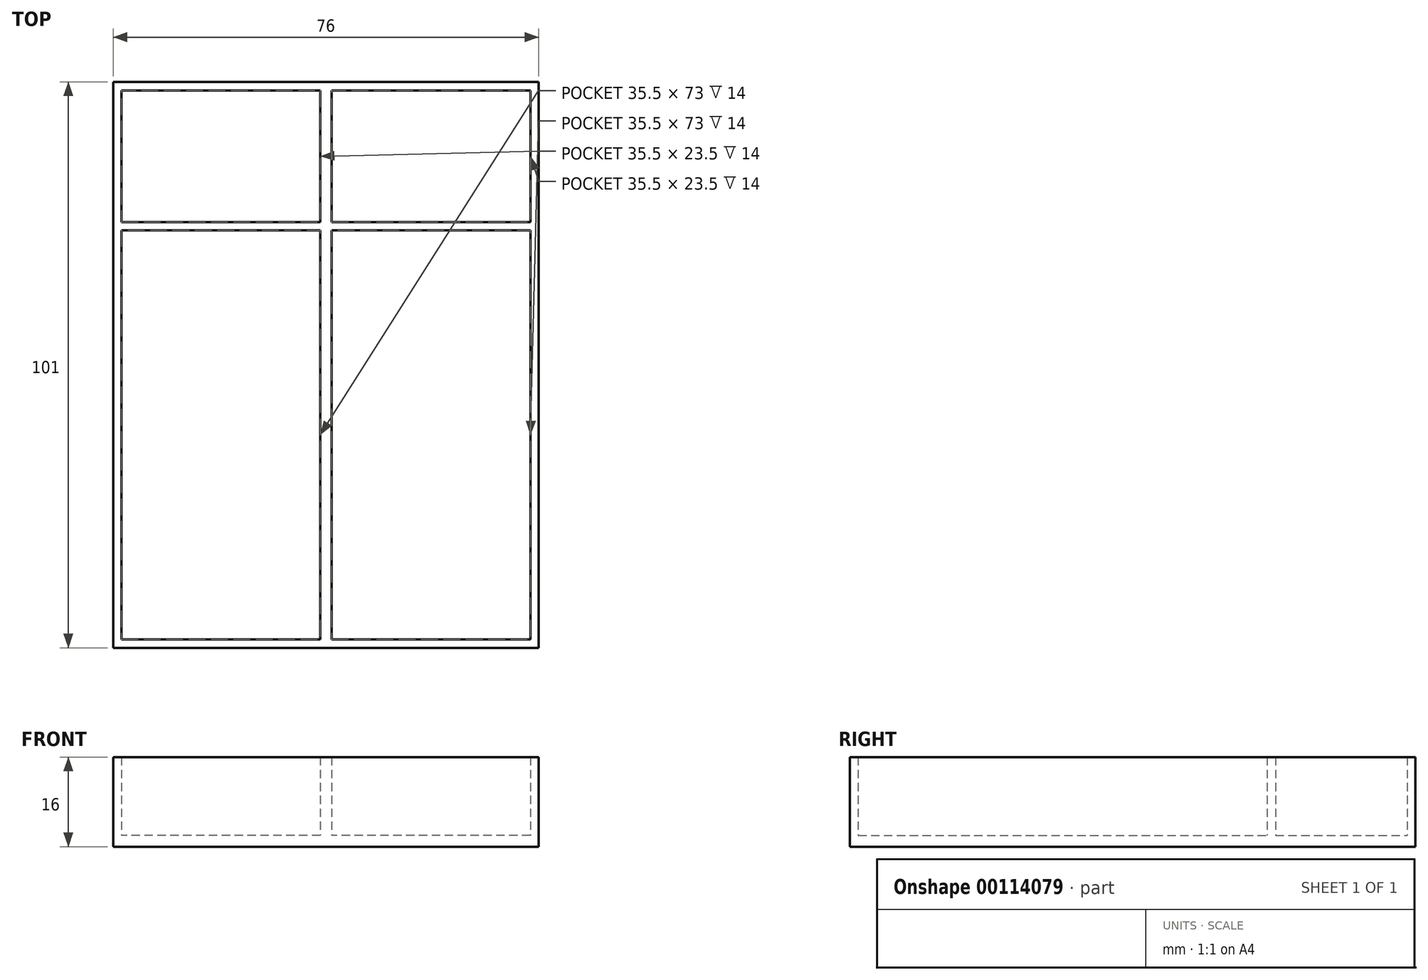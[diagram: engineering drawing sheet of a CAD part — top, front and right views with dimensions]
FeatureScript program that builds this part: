
annotation { "Feature Type Name" : "Feature", "Feature Type Description" : "" }
export const myFeature = defineFeature(function(context is Context, id is Id, definition is map)
    precondition{}
    {
        {
            var Q0;
            Q0=qCreatedBy(makeId("Top.planeOp"),FACE);
            var sketch = newSketch(context, id + "F0", { "sketchPlane" : qUnion([Q0])});
            skLineSegment(sketch, "E0.bottom", {"start": v(38, -38) * mm, "end": v(-38, -38) * mm});
            skLineSegment(sketch, "E0.top", {"start": v(38, 38) * mm, "end": v(-38, 38) * mm});
            skLineSegment(sketch, "E0.left", {"start": v(38, -38) * mm, "end": v(38, 38) * mm});
            skLineSegment(sketch, "E0.right", {"start": v(-38, -38) * mm, "end": v(-38, 38) * mm});
            skPoint(sketch, "E0.middle", {"position": v(0, 0) * mm});
            skLineSegment(sketch, "E1.bottom", {"start": v(-38, 38) * mm, "end": v(38, 38) * mm});
            skLineSegment(sketch, "E1.top", {"start": v(-38, 63) * mm, "end": v(38, 63) * mm});
            skLineSegment(sketch, "E1.left", {"start": v(-38, 38) * mm, "end": v(-38, 63) * mm});
            skLineSegment(sketch, "E1.right", {"start": v(38, 38) * mm, "end": v(38, 63) * mm});
            skLineSegment(sketch, "E2", {"start": v(-36.5, 38) * mm, "end": v(-36.5, 61.5) * mm});
            skLineSegment(sketch, "E3", {"start": v(-36.5, 61.5) * mm, "end": v(-1, 61.5) * mm});
            skLineSegment(sketch, "E4", {"start": v(36.5, 61.5) * mm, "end": v(36.5, 38) * mm});
            skLineSegment(sketch, "E5", {"start": v(-1, 38) * mm, "end": v(-1, 61.5) * mm});
            skLineSegment(sketch, "E6", {"start": v(1, 38) * mm, "end": v(1, 61.5) * mm});
            skLineSegment(sketch, "E7.trimOffspring", {"start": v(1, 61.5) * mm, "end": v(36.5, 61.5) * mm});
            skSolve(sketch);
        }
        {
            var Q0;
            Q0=makeQuery(id+"F0.imprint","IMPRINT",FACE,{"disambiguationData":[TD([[makeQuery(id+"F0.imprint","IMPRINT",EDGE,{"derivedFrom":sQuery(id+"F0.wireOp",EDGE,"E0.bottom")}),-1.0]])]});
            var sketch = newSketch(context, id + "F1", { "sketchPlane" : qUnion([Q0])});
            skLineSegment(sketch, "E8.bottom", {"start": v(36.5, -36.5) * mm, "end": v(-36.5, -36.5) * mm});
            skLineSegment(sketch, "E8.top", {"start": v(36.5, 36.5) * mm, "end": v(-36.5, 36.5) * mm});
            skLineSegment(sketch, "E8.left", {"start": v(36.5, -36.5) * mm, "end": v(36.5, 36.5) * mm});
            skLineSegment(sketch, "E8.right", {"start": v(-36.5, -36.5) * mm, "end": v(-36.5, 36.5) * mm});
            skPoint(sketch, "E8.middle", {"position": v(0, 0) * mm});
            skSolve(sketch);
        }
        {
            var Q0;
            Q0=makeQuery(id+"F1.imprint","IMPRINT",FACE,{"disambiguationData":[TD([[makeQuery(id+"F1.imprint","IMPRINT",EDGE,{"derivedFrom":sQuery(id+"F1.wireOp",EDGE,"E8.bottom")}),1.0]])]});
            extrude(context, id + "F2", {"entities" : qUnion([Q0]), "depth" : 16 * mm});
        }
        {
            var Q0;
            Q0=makeQuery(id+"F0.imprint","IMPRINT",FACE,{"disambiguationData":[TD([[makeQuery(id+"F0.imprint","IMPRINT",EDGE,{"derivedFrom":sQuery(id+"F0.wireOp",EDGE,"E0.bottom")}),-1.0]])]});
            extrude(context, id + "F3", {"entities" : qUnion([Q0]), "operationType" : NewBodyOperationType.ADD, "depth" : 2 * mm});
        }
        {
            var Q0;
            Q0=makeQuery(id+"F3.opExtrude","CAP_FACE",FACE,{"disambiguationData":[OSD([sQuery(id+"F0.wireOp",EDGE,"E0.bottom"),sQuery(id+"F0.wireOp",EDGE,"E0.top"),sQuery(id+"F0.wireOp",EDGE,"E0.left"),sQuery(id+"F0.wireOp",EDGE,"E0.right")])],"isStart":false});
            var sketch = newSketch(context, id + "F4", { "sketchPlane" : qUnion([Q0])});
            skLineSegment(sketch, "E9.bottom", {"start": v(1, -36.5) * mm, "end": v(-1, -36.5) * mm});
            skLineSegment(sketch, "E9.top", {"start": v(1, 36.5) * mm, "end": v(-1, 36.5) * mm});
            skLineSegment(sketch, "E9.left", {"start": v(1, -36.5) * mm, "end": v(1, 36.5) * mm});
            skLineSegment(sketch, "E9.right", {"start": v(-1, -36.5) * mm, "end": v(-1, 36.5) * mm});
            skPoint(sketch, "E9.middle", {"position": v(0, 0) * mm});
            skSolve(sketch);
        }
        {
            var Q0;
            Q0=makeQuery(id+"F4.imprint","IMPRINT",FACE,{"disambiguationData":[TD([[makeQuery(id+"F4.imprint","IMPRINT",EDGE,{"derivedFrom":sQuery(id+"F4.wireOp",EDGE,"E9.bottom")}),-1.0]])]});
            extrude(context, id + "F5", {"entities" : qUnion([Q0]), "operationType" : NewBodyOperationType.ADD, "depth" : 14 * mm});
        }
        {
            var Q0;
            {var subQ0=sQuery(id+"F0.wireOp",EDGE,"E2");Q0=makeQuery(id+"F0.imprint","IMPRINT",FACE,{"disambiguationData":[TD([[makeQuery(id+"F0.imprint","IMPRINT",EDGE,{"derivedFrom":subQ0}),-1.0]])]});}
            extrude(context, id + "F6", {"entities" : qUnion([Q0]), "operationType" : NewBodyOperationType.ADD, "depth" : 2 * mm});
        }
        {
            var Q0;
            {var subQ0=sQuery(id+"F0.wireOp",EDGE,"E4");Q0=makeQuery(id+"F0.imprint","IMPRINT",FACE,{"disambiguationData":[TD([[makeQuery(id+"F0.imprint","IMPRINT",EDGE,{"derivedFrom":subQ0}),-1.0]])]});}
            extrude(context, id + "F7", {"entities" : qUnion([Q0]), "operationType" : NewBodyOperationType.ADD, "depth" : 2 * mm});
        }
        {
            var Q0;
            Q0=makeQuery(id+"F0.imprint","IMPRINT",FACE,{"disambiguationData":[TD([[makeQuery(id+"F0.imprint","IMPRINT",EDGE,{"derivedFrom":sQuery(id+"F0.wireOp",EDGE,"E1.top")}),-1.0]])]});
            extrude(context, id + "F8", {"entities" : qUnion([Q0]), "operationType" : NewBodyOperationType.ADD, "depth" : 16 * mm});
        }
    });
